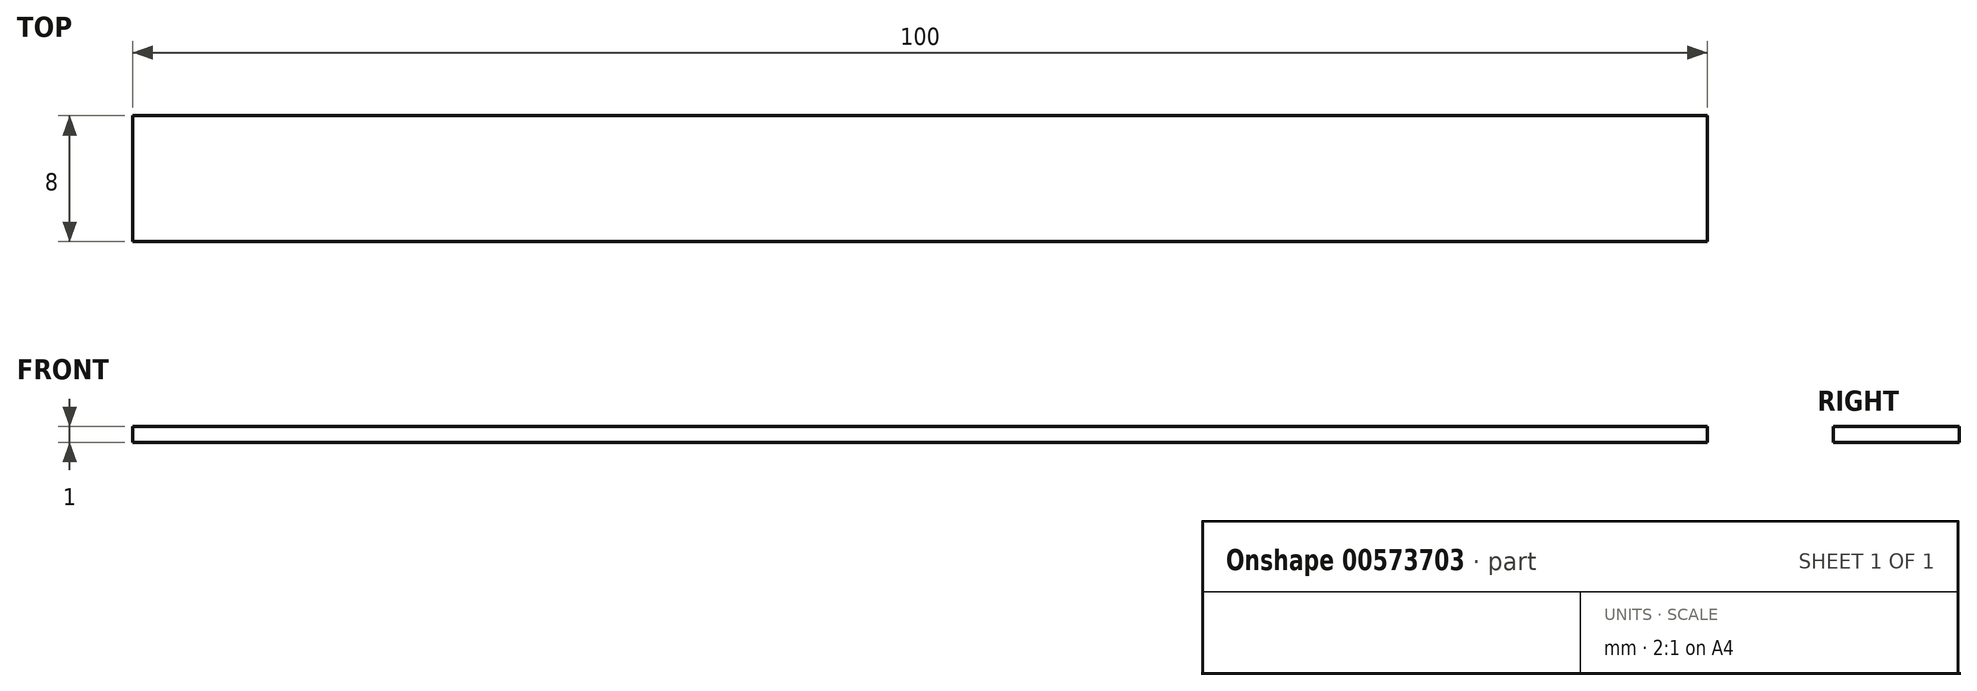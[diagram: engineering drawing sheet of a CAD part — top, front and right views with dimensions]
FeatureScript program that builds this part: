
annotation { "Feature Type Name" : "Feature", "Feature Type Description" : "" }
export const myFeature = defineFeature(function(context is Context, id is Id, definition is map)
    precondition{}
    {
        {
            var Q0;
            Q0=qCreatedBy(makeId("Top.planeOp"),FACE);
            var sketch = newSketch(context, id + "F0", { "sketchPlane" : qUnion([Q0])});
            skLineSegment(sketch, "E0.rect.bottom", {"start": v(50, 4) * mm, "end": v(-50, 4) * mm});
            skLineSegment(sketch, "E0.rect.top", {"start": v(50, -4) * mm, "end": v(-50, -4) * mm});
            skLineSegment(sketch, "E0.rect.left", {"start": v(50, 4) * mm, "end": v(50, -4) * mm});
            skLineSegment(sketch, "E0.rect.right", {"start": v(-50, 4) * mm, "end": v(-50, -4) * mm});
            skPoint(sketch, "E0.rect.middle", {"position": v(0, 0) * mm});
            skSolve(sketch);
        }
        {
            var Q0;
            Q0=qSketchRegion(id+"F0",true);
            extrude(context, id + "F1", {"entities" : qUnion([Q0]), "depth" : 1 * mm});
        }
    });
